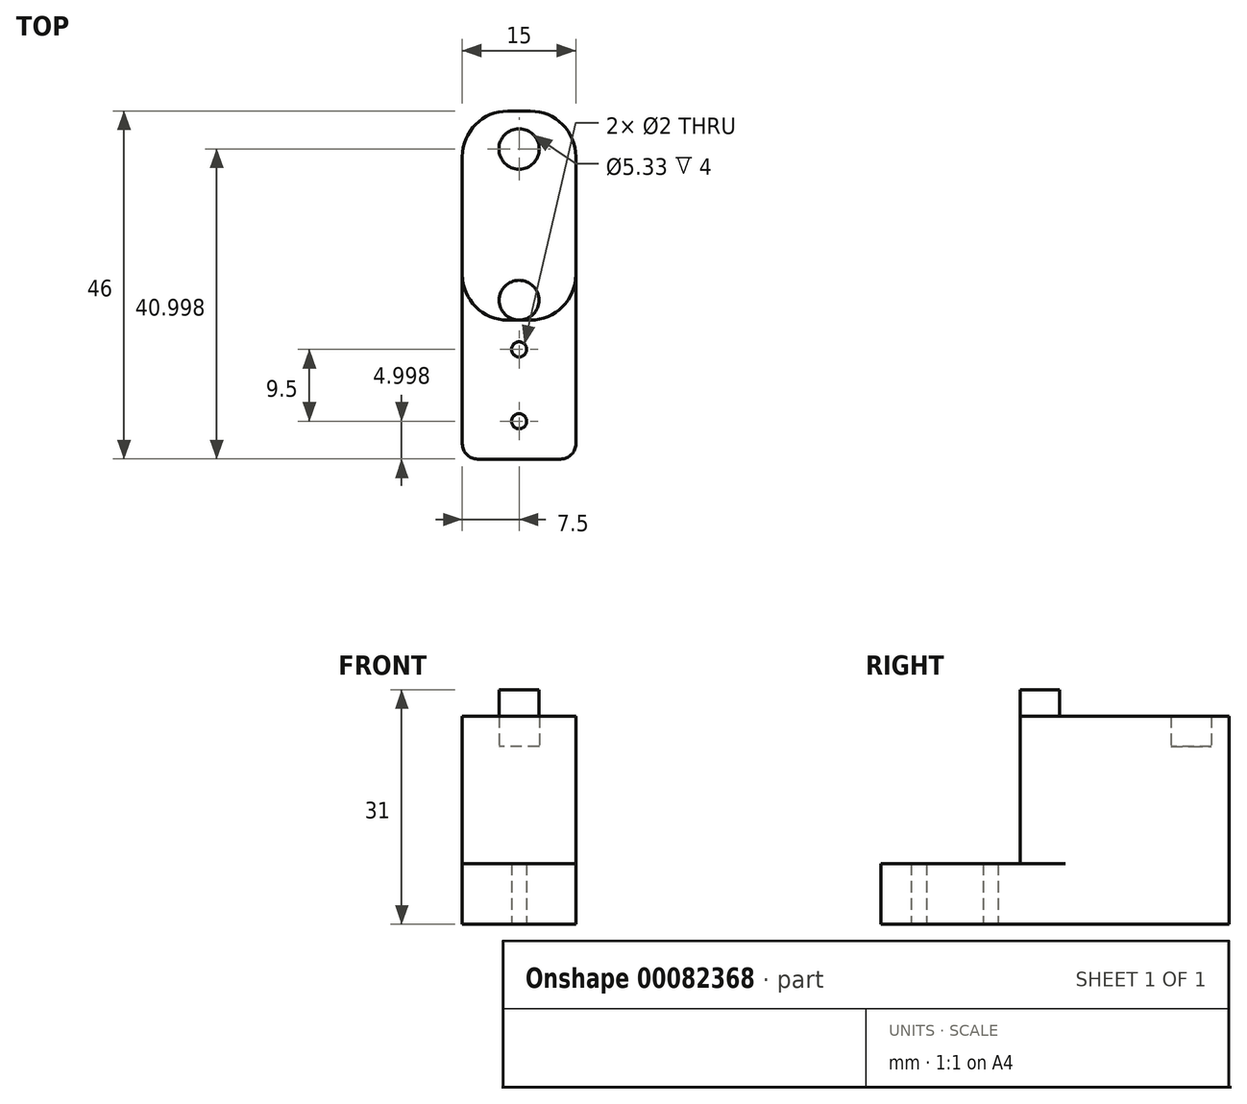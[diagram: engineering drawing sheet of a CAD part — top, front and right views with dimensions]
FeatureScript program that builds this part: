
annotation { "Feature Type Name" : "Feature", "Feature Type Description" : "" }
export const myFeature = defineFeature(function(context is Context, id is Id, definition is map)
    precondition{}
    {
        {
            var Q0;
            Q0=qCreatedBy(makeId("Top.planeOp"),FACE);
            var sketch = newSketch(context, id + "F0", { "sketchPlane" : qUnion([Q0])});
            skCircle(sketch, "E0", {"center": v(0, 20.68) * mm, "radius": 1 * mm});
            skCircle(sketch, "E1", {"center": v(0, 11.18) * mm, "radius": 1 * mm});
            skCircle(sketch, "E2", {"center": v(0, 27.18) * mm, "radius": 2.62 * mm});
            skCircle(sketch, "E3", {"center": v(0, 47.18) * mm, "radius": 2.67 * mm});
            skLineSegment(sketch, "E4.bottom", {"start": v(-1.5, 52.18) * mm, "end": v(1.5, 52.18) * mm});
            skLineSegment(sketch, "E4.top", {"start": v(-5.5, 6.18) * mm, "end": v(5.5, 6.18) * mm});
            skLineSegment(sketch, "E4.left", {"start": v(-7.5, 46.18) * mm, "end": v(-7.5, 30.55) * mm});
            skLineSegment(sketch, "E4.right", {"start": v(7.5, 46.18) * mm, "end": v(7.5, 30.55) * mm});
            skLineSegment(sketch, "E5", {"start": v(-7.5, 30.55) * mm, "end": v(-7.5, 8.18) * mm});
            skLineSegment(sketch, "E6", {"start": v(7.5, 30.55) * mm, "end": v(7.5, 8.18) * mm});
            skPoint(sketch, "E7", {"position": v(0, 6.18) * mm});
            skPoint(sketch, "E8.visualSharp", {"position": v(-7.5, 52.18) * mm});
            skArc(sketch, "E8.filletArc", {"start": v(-1.5, 52.18) * mm, "mid": v(-5.74, 50.42) * mm, "end": v(-7.5, 46.18) * mm});
            skPoint(sketch, "E9.visualSharp", {"position": v(7.5, 52.18) * mm});
            skArc(sketch, "E9.filletArc", {"start": v(7.5, 46.18) * mm, "mid": v(5.74, 50.42) * mm, "end": v(1.5, 52.18) * mm});
            skLineSegment(sketch, "E10", {"start": v(-1.5, 24.55) * mm, "end": v(1.5, 24.55) * mm});
            skPoint(sketch, "E11.visualSharp", {"position": v(-7.5, 6.18) * mm});
            skArc(sketch, "E11.filletArc", {"start": v(-7.5, 8.18) * mm, "mid": v(-6.91, 6.76) * mm, "end": v(-5.5, 6.18) * mm});
            skPoint(sketch, "E12.visualSharp", {"position": v(7.5, 6.18) * mm});
            skArc(sketch, "E12.filletArc", {"start": v(5.5, 6.18) * mm, "mid": v(6.91, 6.76) * mm, "end": v(7.5, 8.18) * mm});
            skArc(sketch, "E13.filletArc", {"start": v(-7.5, 30.55) * mm, "mid": v(-5.74, 26.31) * mm, "end": v(-1.5, 24.55) * mm});
            skArc(sketch, "E14.filletArc", {"start": v(1.5, 24.55) * mm, "mid": v(5.74, 26.31) * mm, "end": v(7.5, 30.55) * mm});
            skSolve(sketch);
        }
        {
            assignVariable(context, id + "F1", {"name" : "width", "anyValue" : 27.5});
        }
        {
            var Q0;
            Q0=makeQuery(id+"F0.imprint","IMPRINT",FACE,{"disambiguationData":[TD([[makeQuery(id+"F0.imprint","IMPRINT",EDGE,{"derivedFrom":sQuery(id+"F0.wireOp",EDGE,"E0")}),-1.0]])]});
            extrude(context, id + "F2", {"entities" : qUnion([Q0]), "depth" : 8 * mm});
        }
        {
            var Q0;
            {var subQ3=sQuery(id+"F0.wireOp",EDGE,"E2");Q0=makeQuery(id+"F0.imprint","IMPRINT",FACE,{"disambiguationData":[TD([[makeQuery(id+"F0.imprint","IMPRINT",EDGE,{"derivedFrom":subQ3}),-1.0]])]});}
            var Q1;
            Q1=makeQuery(id+"F0.imprint","IMPRINT",FACE,{"disambiguationData":[TD([[makeQuery(id+"F0.imprint","IMPRINT",EDGE,{"derivedFrom":sQuery(id+"F0.wireOp",EDGE,"E2")}),1.0]])]});
            extrude(context, id + "F3", {"entities" : qUnion([Q0, Q1]), "operationType" : NewBodyOperationType.ADD, "depth" : (getVariable(context, 'width')) * mm});
        }
        {
            var Q0;
            Q0=makeQuery(id+"F0.imprint","IMPRINT",FACE,{"disambiguationData":[TD([[makeQuery(id+"F0.imprint","IMPRINT",EDGE,{"derivedFrom":sQuery(id+"F0.wireOp",EDGE,"E2")}),1.0]])]});
            extrude(context, id + "F4", {"entities" : qUnion([Q0]), "operationType" : NewBodyOperationType.ADD, "depth" : (getVariable(context, 'width') + 3.5) * mm});
        }
        {
            var Q0;
            Q0=makeQuery(id+"F0.imprint","IMPRINT",FACE,{"disambiguationData":[TD([[makeQuery(id+"F0.imprint","IMPRINT",EDGE,{"derivedFrom":sQuery(id+"F0.wireOp",EDGE,"E3")}),1.0]])]});
            var Q1;
            Q1=makeQuery(id+"F3.opExtrude","CAP_FACE",FACE,{"disambiguationData":[OSD([sQuery(id+"F0.wireOp",EDGE,"E4.bottom"),sQuery(id+"F0.wireOp",EDGE,"E4.left"),sQuery(id+"F0.wireOp",EDGE,"E4.right"),sQuery(id+"F0.wireOp",EDGE,"E8.filletArc"),sQuery(id+"F0.wireOp",EDGE,"E9.filletArc"),sQuery(id+"F0.wireOp",EDGE,"E10")])],"isStart":false});
            extrude(context, id + "F5", {"entities" : qUnion([Q0]), "operationType" : NewBodyOperationType.ADD, "endBoundEntityFace" : qUnion([Q1]), "depth" : (getVariable(context, 'width') - 4) * mm});
        }
    });
